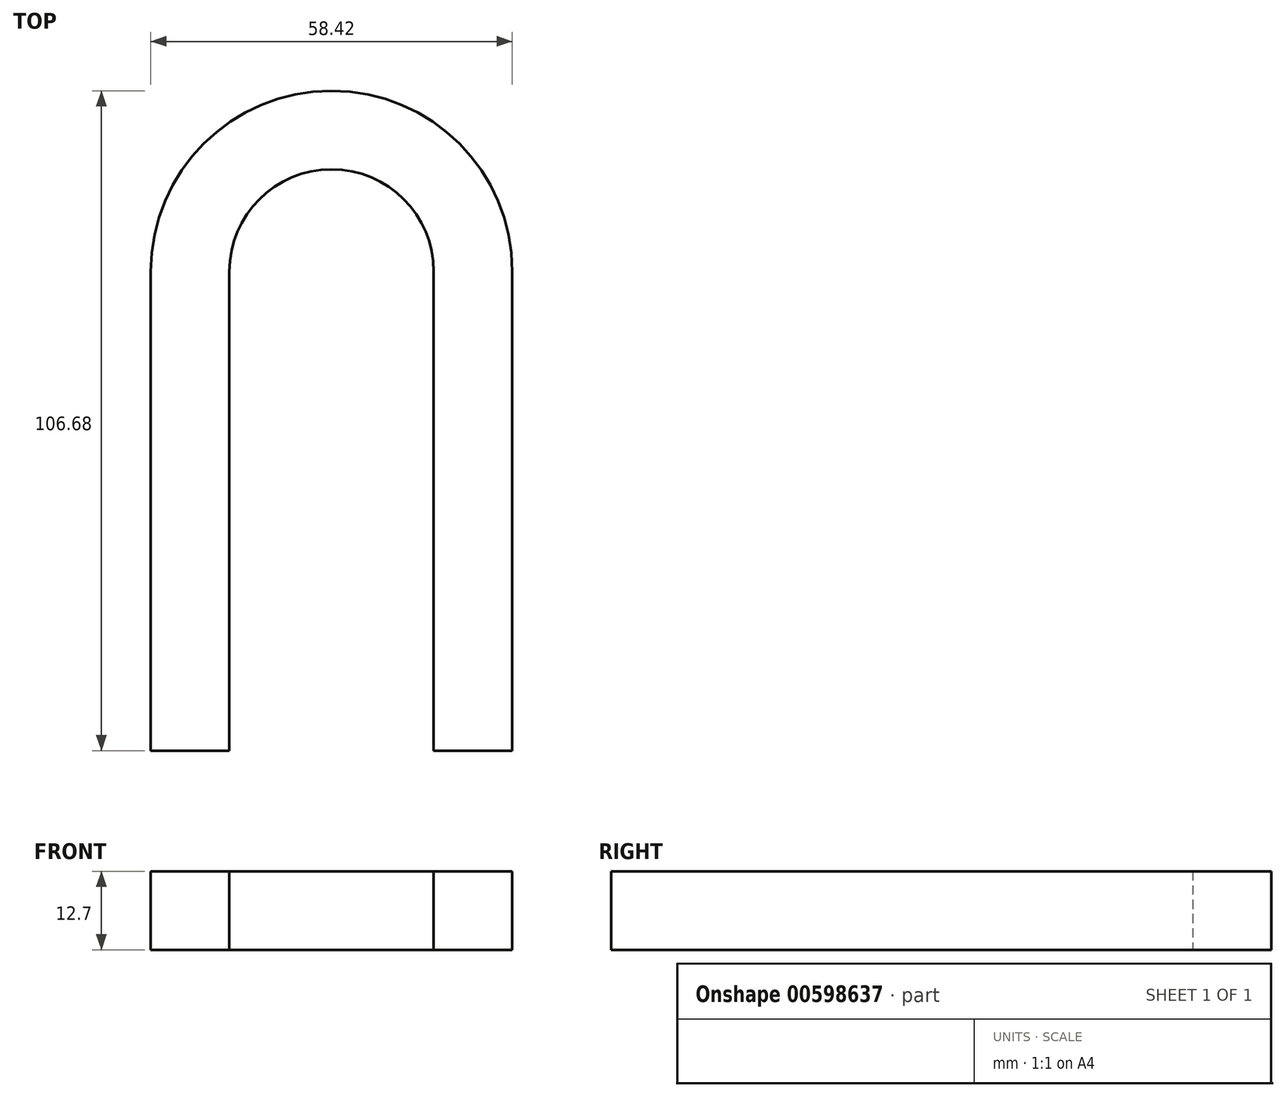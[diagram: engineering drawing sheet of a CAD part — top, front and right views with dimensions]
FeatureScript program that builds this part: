
annotation { "Feature Type Name" : "Feature", "Feature Type Description" : "" }
export const myFeature = defineFeature(function(context is Context, id is Id, definition is map)
    precondition{}
    {
        {
            var Q0;
            Q0=qCreatedBy(makeId("Top.planeOp"),FACE);
            var sketch = newSketch(context, id + "F0", { "sketchPlane" : qUnion([Q0])});
            skArc(sketch, "E0", {"start": v(-2.63, 32.83) * mm, "mid": v(-19.14, 49.34) * mm, "end": v(-35.65, 32.83) * mm});
            skArc(sketch, "E1", {"start": v(10.07, 32.83) * mm, "mid": v(-19.14, 62.04) * mm, "end": v(-48.35, 32.83) * mm});
            skLineSegment(sketch, "E2", {"start": v(-19.14, 32.83) * mm, "end": v(-72.75, 32.83) * mm, "construction": true});
            skLineSegment(sketch, "E3", {"start": v(-72.75, 32.83) * mm, "end": v(18.02, 32.83) * mm, "construction": true});
            skLineSegment(sketch, "E4", {"start": v(-48.35, 32.83) * mm, "end": v(-48.35, -6.54) * mm});
            skLineSegment(sketch, "E5", {"start": v(10.07, 32.83) * mm, "end": v(10.07, -6.54) * mm});
            skLineSegment(sketch, "E6", {"start": v(-35.65, 32.83) * mm, "end": v(-35.65, -6.54) * mm});
            skLineSegment(sketch, "E7", {"start": v(-2.63, 32.83) * mm, "end": v(-2.63, -6.54) * mm});
            skLineSegment(sketch, "E8", {"start": v(-48.35, -6.54) * mm, "end": v(-48.35, -44.64) * mm});
            skLineSegment(sketch, "E9", {"start": v(-35.65, -6.54) * mm, "end": v(-35.65, -44.64) * mm});
            skLineSegment(sketch, "E10", {"start": v(-2.63, -6.54) * mm, "end": v(-2.63, -44.64) * mm});
            skLineSegment(sketch, "E11", {"start": v(-48.35, -44.64) * mm, "end": v(-35.65, -44.64) * mm});
            skLineSegment(sketch, "E12", {"start": v(-2.63, -44.64) * mm, "end": v(10.07, -44.64) * mm});
            skLineSegment(sketch, "E13", {"start": v(10.07, -6.54) * mm, "end": v(10.07, -44.64) * mm});
            skSolve(sketch);
        }
        {
            var Q0;
            Q0 = qSketchRegion(id + "F0", true);
            extrude(context, id + "F1", {"entities" : qUnion([Q0]), "depth" : 12.7 * mm, "offsetDistance" : 25.4 * mm});
        }
    });
